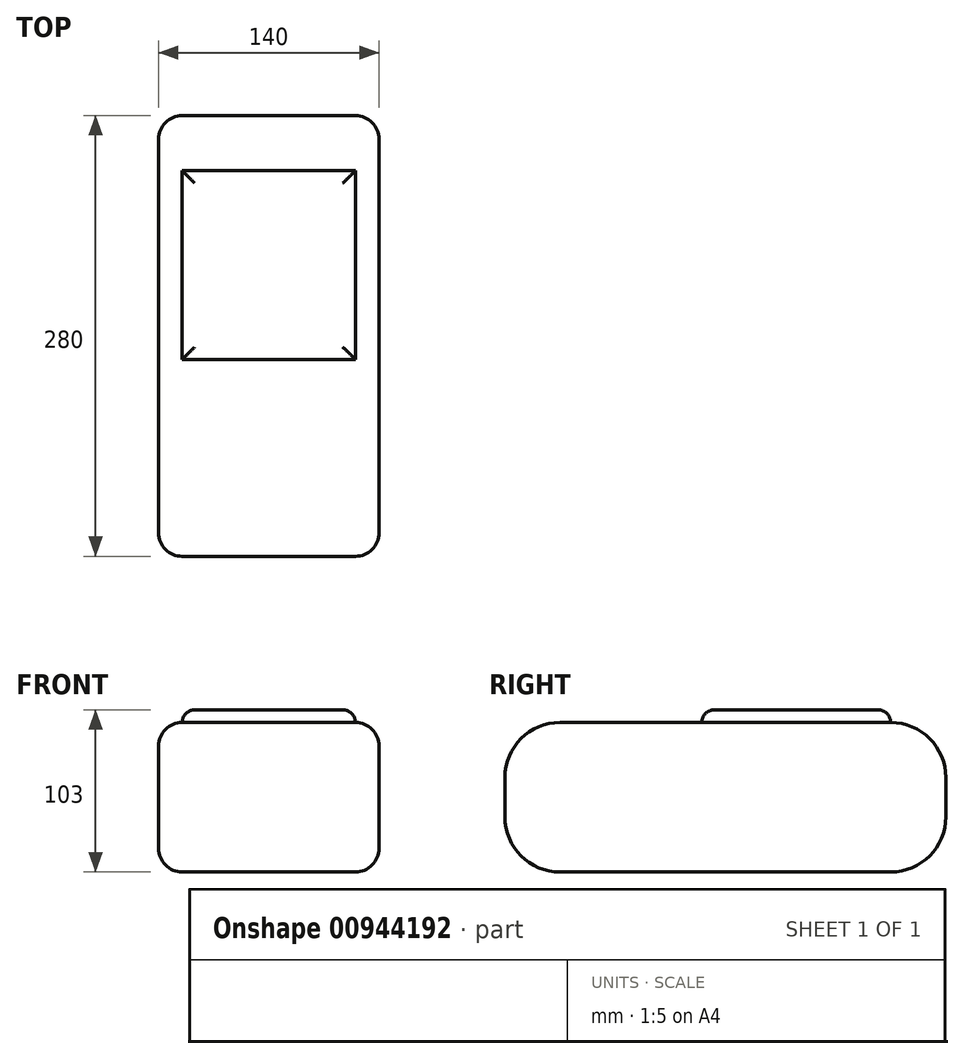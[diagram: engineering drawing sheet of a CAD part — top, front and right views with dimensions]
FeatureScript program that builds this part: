
annotation { "Feature Type Name" : "Feature", "Feature Type Description" : "" }
export const myFeature = defineFeature(function(context is Context, id is Id, definition is map)
    precondition{}
    {
        {
            var Q0;
            Q0=qCreatedBy(makeId("Top.planeOp"),FACE);
            var sketch = newSketch(context, id + "F0", { "sketchPlane" : qUnion([Q0])});
            skLineSegment(sketch, "E0.bottom", {"start": v(70, -140) * mm, "end": v(-70, -140) * mm});
            skLineSegment(sketch, "E0.top", {"start": v(70, 140) * mm, "end": v(-70, 140) * mm});
            skLineSegment(sketch, "E0.left", {"start": v(70, -140) * mm, "end": v(70, 140) * mm});
            skLineSegment(sketch, "E0.right", {"start": v(-70, -140) * mm, "end": v(-70, 140) * mm});
            skPoint(sketch, "E0.middle", {"position": v(0, 0) * mm});
            skSolve(sketch);
        }
        {
            var Q0;
            Q0 = qSketchRegion(id + "F0", true);
            extrude(context, id + "F1", {"entities" : qUnion([Q0]), "depth" : 95 * mm, "offsetDistance" : 25 * mm});
        }
        {
            var Q0;
            Q0=makeQuery(id+"F1.opExtrude","SWEPT_FACE",FACE,{"disambiguationData":[OSD([sQuery(id+"F0.wireOp",EDGE,"E0.left")])]});
            var Q1;
            Q1=makeQuery(id+"F1.opExtrude","SWEPT_FACE",FACE,{"disambiguationData":[OSD([sQuery(id+"F0.wireOp",EDGE,"E0.right")])]});
            fillet(context, id + "F2", {"entities" : qUnion([Q0, Q1]), "radius" : 15 * mm, "tangentPropagation" : true, "allowEdgeOverflow" : false});
        }
        {
            var Q0;
            Q0=makeQuery(id+"F1.opExtrude","CAP_EDGE",EDGE,{"disambiguationData":[OSD([sQuery(id+"F0.wireOp",EDGE,"E0.bottom")])],"isStart":false});
            var Q1;
            Q1=makeQuery(id+"F1.opExtrude","CAP_EDGE",EDGE,{"disambiguationData":[OSD([sQuery(id+"F0.wireOp",EDGE,"E0.bottom")])],"isStart":true});
            var Q2;
            Q2=makeQuery(id+"F1.opExtrude","CAP_EDGE",EDGE,{"disambiguationData":[OSD([sQuery(id+"F0.wireOp",EDGE,"E0.top")])],"isStart":false});
            var Q3;
            Q3=makeQuery(id+"F1.opExtrude","CAP_EDGE",EDGE,{"disambiguationData":[OSD([sQuery(id+"F0.wireOp",EDGE,"E0.top")])],"isStart":true});
            fillet(context, id + "F3", {"entities" : qUnion([Q0, Q1, Q2, Q3]), "radius" : 35 * mm, "tangentPropagation" : true, "allowEdgeOverflow" : false});
        }
        {
            var Q0;
            Q0=makeQuery(id+"F1.opExtrude","CAP_FACE",FACE,{"disambiguationData":[OSD([sQuery(id+"F0.wireOp",EDGE,"E0.bottom"),sQuery(id+"F0.wireOp",EDGE,"E0.top"),sQuery(id+"F0.wireOp",EDGE,"E0.left"),sQuery(id+"F0.wireOp",EDGE,"E0.right")])],"isStart":false});
            var sketch = newSketch(context, id + "F4", { "sketchPlane" : qUnion([Q0])});
            skLineSegment(sketch, "E1.bottom", {"start": v(-55, 105) * mm, "end": v(55, 105) * mm});
            skLineSegment(sketch, "E1.top", {"start": v(-55, -15) * mm, "end": v(55, -15) * mm});
            skLineSegment(sketch, "E1.left", {"start": v(-55, 105) * mm, "end": v(-55, -15) * mm});
            skLineSegment(sketch, "E1.right", {"start": v(55, 105) * mm, "end": v(55, -15) * mm});
            skSolve(sketch);
        }
        {
            var Q0;
            Q0 = qSketchRegion(id + "F4", true);
            extrude(context, id + "F5", {"entities" : qUnion([Q0]), "operationType" : NewBodyOperationType.ADD, "depth" : 8 * mm, "offsetDistance" : 25 * mm});
        }
        {
            var Q0;
            Q0=makeQuery(id+"F5.opExtrude","CAP_FACE",FACE,{"disambiguationData":[OSD([sQuery(id+"F4.wireOp",EDGE,"E1.bottom"),sQuery(id+"F4.wireOp",EDGE,"E1.top"),sQuery(id+"F4.wireOp",EDGE,"E1.left"),sQuery(id+"F4.wireOp",EDGE,"E1.right")])],"isStart":false});
            fillet(context, id + "F6", {"entities" : qUnion([Q0]), "radius" : 8 * mm, "tangentPropagation" : true, "allowEdgeOverflow" : false});
        }
    });
